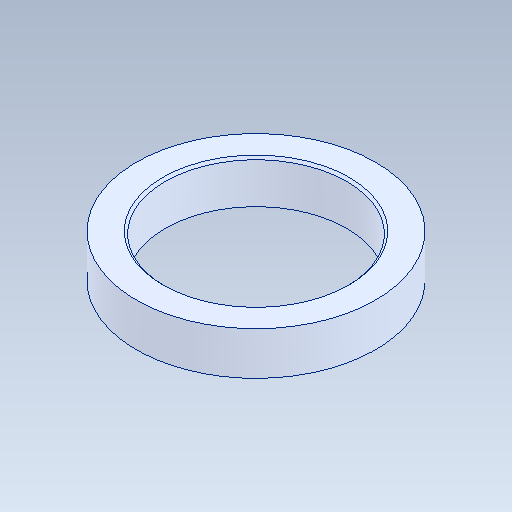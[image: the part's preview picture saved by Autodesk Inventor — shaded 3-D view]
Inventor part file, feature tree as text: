
AUTODESK INVENTOR PART (.ipt)
format: ipt  version: 2020 (Build 240168000, 168)  size: 93,184 bytes
history: native  units: in
note: dims shown in document units (in); Inventor stores cm internally (conversion verified against a paired STEP export)
features: chamfer x1
ambient origin geometry x8: Origin, YZ Plane, XZ Plane, XY Plane, X Axis, Y Axis, Z Axis, Center Point
bodies: Solid1 (feature_tree)
feature tree (1):
  chamfer  "Chamfer1"  [1 undecoded]
note: 1 required parameter value undecoded (feature->parameter linkage not recoverable at this tier; creation-order binding heuristic only, values carry confidence <= 0.55)
